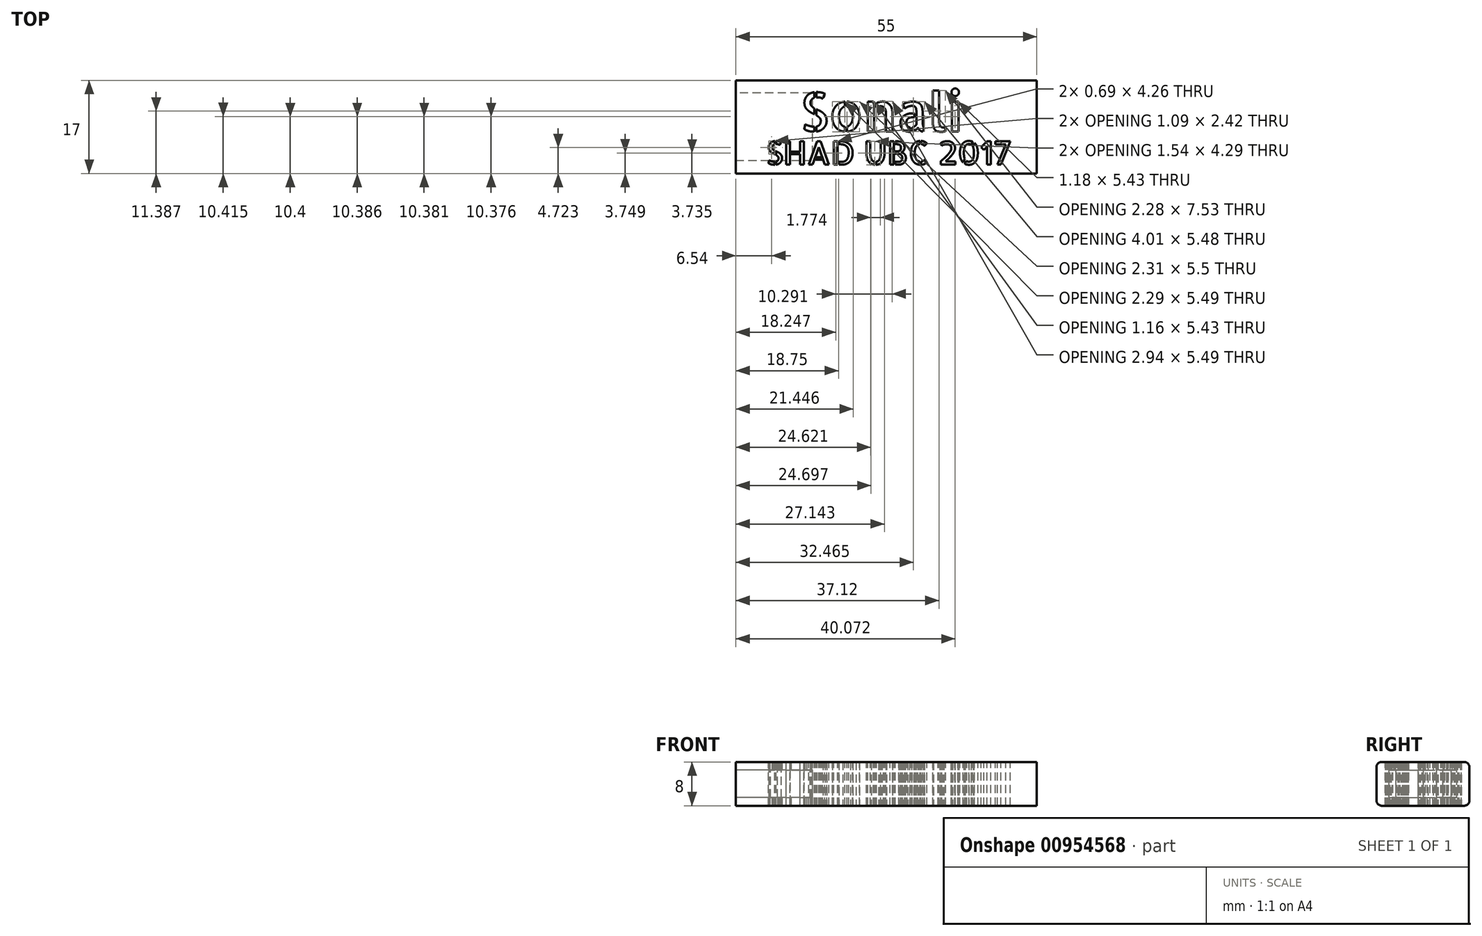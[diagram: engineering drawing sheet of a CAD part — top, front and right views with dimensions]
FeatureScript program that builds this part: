
annotation { "Feature Type Name" : "Feature", "Feature Type Description" : "" }
export const myFeature = defineFeature(function(context is Context, id is Id, definition is map)
    precondition{}
    {
        {
            var Q0;
            Q0=qCreatedBy(makeId("Front.planeOp"),FACE);
            var sketch = newSketch(context, id + "F0", { "sketchPlane" : qUnion([Q0])});
            skLineSegment(sketch, "E0.bottom", {"start": v(-7.5, 4) * mm, "end": v(7.5, 4) * mm});
            skLineSegment(sketch, "E0.top", {"start": v(-7.5, -4) * mm, "end": v(7.5, -4) * mm});
            skLineSegment(sketch, "E0.left", {"start": v(-8.5, 3) * mm, "end": v(-8.5, -3) * mm});
            skLineSegment(sketch, "E0.right", {"start": v(8.5, 3) * mm, "end": v(8.5, -3) * mm});
            skPoint(sketch, "E0.middle", {"position": v(0, 0) * mm});
            skPoint(sketch, "E1.visualSharp", {"position": v(-8.5, 4) * mm});
            skArc(sketch, "E1.filletArc", {"start": v(-7.5, 4) * mm, "mid": v(-8.2, 3.7) * mm, "end": v(-8.5, 3) * mm});
            skPoint(sketch, "E2.visualSharp", {"position": v(8.5, 4) * mm});
            skArc(sketch, "E2.filletArc", {"start": v(8.5, 3) * mm, "mid": v(8.2, 3.7) * mm, "end": v(7.5, 4) * mm});
            skPoint(sketch, "E3.visualSharp", {"position": v(8.5, -4) * mm});
            skArc(sketch, "E3.filletArc", {"start": v(7.5, -4) * mm, "mid": v(8.2, -3.7) * mm, "end": v(8.5, -3) * mm});
            skPoint(sketch, "E4.visualSharp", {"position": v(-8.5, -4) * mm});
            skArc(sketch, "E4.filletArc", {"start": v(-8.5, -3) * mm, "mid": v(-8.2, -3.7) * mm, "end": v(-7.5, -4) * mm});
            skSolve(sketch);
        }
        {
            var Q0;
            Q0 = qSketchRegion(id + "F0", true);
            extrude(context, id + "F1", {"entities" : qUnion([Q0]), "depth" : 55 * mm, "offsetDistance" : 25 * mm});
        }
        {
            var Q0;
            Q0=makeQuery(id+"F1.opExtrude","CAP_FACE",FACE,{"disambiguationData":[OSD([sQuery(id+"F0.wireOp",EDGE,"E0.bottom"),sQuery(id+"F0.wireOp",EDGE,"E0.top"),sQuery(id+"F0.wireOp",EDGE,"E0.left"),sQuery(id+"F0.wireOp",EDGE,"E0.right"),sQuery(id+"F0.wireOp",EDGE,"E1.filletArc"),sQuery(id+"F0.wireOp",EDGE,"E2.filletArc"),sQuery(id+"F0.wireOp",EDGE,"E3.filletArc"),sQuery(id+"F0.wireOp",EDGE,"E4.filletArc")])],"isStart":false});
            var sketch = newSketch(context, id + "F2", { "sketchPlane" : qUnion([Q0])});
            skLineSegment(sketch, "E5.bottom", {"start": v(6.2, -2.5) * mm, "end": v(-6.2, -2.5) * mm});
            skLineSegment(sketch, "E5.top", {"start": v(6.2, 2.5) * mm, "end": v(-6.2, 2.5) * mm});
            skLineSegment(sketch, "E5.left", {"start": v(6.2, -2.5) * mm, "end": v(6.2, 2.5) * mm});
            skLineSegment(sketch, "E5.right", {"start": v(-6.2, -2.5) * mm, "end": v(-6.2, 2.5) * mm});
            skPoint(sketch, "E5.middle", {"position": v(0, 0) * mm});
            skSolve(sketch);
        }
        {
            var Q0;
            Q0 = qSketchRegion(id + "F2", true);
            extrude(context, id + "F3", {"entities" : qUnion([Q0]), "operationType" : NewBodyOperationType.REMOVE, "oppositeDirection" : true, "depth" : 14 * mm, "offsetDistance" : 25 * mm});
        }
        {
            var Q0;
            Q0=makeQuery(id+"F1.opExtrude","SWEPT_BODY",BODY,{"disambiguationData":[OSD([sQuery(id+"F0.wireOp",EDGE,"E0.bottom"),sQuery(id+"F0.wireOp",EDGE,"E0.top"),sQuery(id+"F0.wireOp",EDGE,"E0.left"),sQuery(id+"F0.wireOp",EDGE,"E0.right"),sQuery(id+"F0.wireOp",EDGE,"E1.filletArc"),sQuery(id+"F0.wireOp",EDGE,"E2.filletArc"),sQuery(id+"F0.wireOp",EDGE,"E3.filletArc"),sQuery(id+"F0.wireOp",EDGE,"E4.filletArc")])]});
            var Q1;
            Q1=makeQuery(id+"F1.opExtrude","CAP_EDGE",EDGE,{"disambiguationData":[OSD([sQuery(id+"F0.wireOp",EDGE,"E0.left")])],"isStart":false});
            transform(context, id + "F4", {"entities" : qUnion([Q0]), "transformType" : TransformType.ROTATION, "transformAxis" : qUnion([Q1]), "angle" : 90 * degree, "makeCopy" : false});
        }
        {
            var Q0;
            Q0=makeQuery(id+"F1.opExtrude","SWEPT_FACE",FACE,{"disambiguationData":[OSD([sQuery(id+"F0.wireOp",EDGE,"E0.bottom")])]});
            var sketch = newSketch(context, id + "F5", { "sketchPlane" : qUnion([Q0])});
            skText(sketch, "E6", { "text": "Sonali", "fontName": "AllertaStencil-Regular.ttf"});
            const initialGuessF5  = {"E6": [0.00319, -0.06433, 1, 0, 0.0071]};
            skSetInitialGuess(sketch, initialGuessF5);
            skSolve(sketch);
        }
        {
            var Q0;
            Q0=makeQuery(id+"F5.imprint","IMPRINT",FACE,{"disambiguationData":[TD([[makeQuery(id+"F5.imprint","IMPRINT",EDGE,{"derivedFrom":sQuery(id+"F5.wireOp",EDGE,"E6.sketch_text.stroke-0")}),1.0]])]});
            var sketch = newSketch(context, id + "F6", { "sketchPlane" : qUnion([Q0])});
            skText(sketch, "E7", { "text": "SHAD UBC 2017 ", "fontName": "AllertaStencil-Regular.ttf"});
            const initialGuessF6  = {"E7": [-0.003, -0.07038, 1, 0, 0.00426]};
            skSetInitialGuess(sketch, initialGuessF6);
            skSolve(sketch);
        }
        {
            var Q0;
            Q0 = qSketchRegion(id + "F5", true);
            extrude(context, id + "F7", {"entities" : qUnion([Q0]), "operationType" : NewBodyOperationType.REMOVE, "oppositeDirection" : true, "depth" : 25 * mm, "offsetDistance" : 25 * mm});
        }
        {
            var Q0;
            Q0 = qSketchRegion(id + "F6", true);
            extrude(context, id + "F8", {"entities" : qUnion([Q0]), "operationType" : NewBodyOperationType.REMOVE, "oppositeDirection" : true, "depth" : 25 * mm, "offsetDistance" : 25 * mm});
        }
    });
